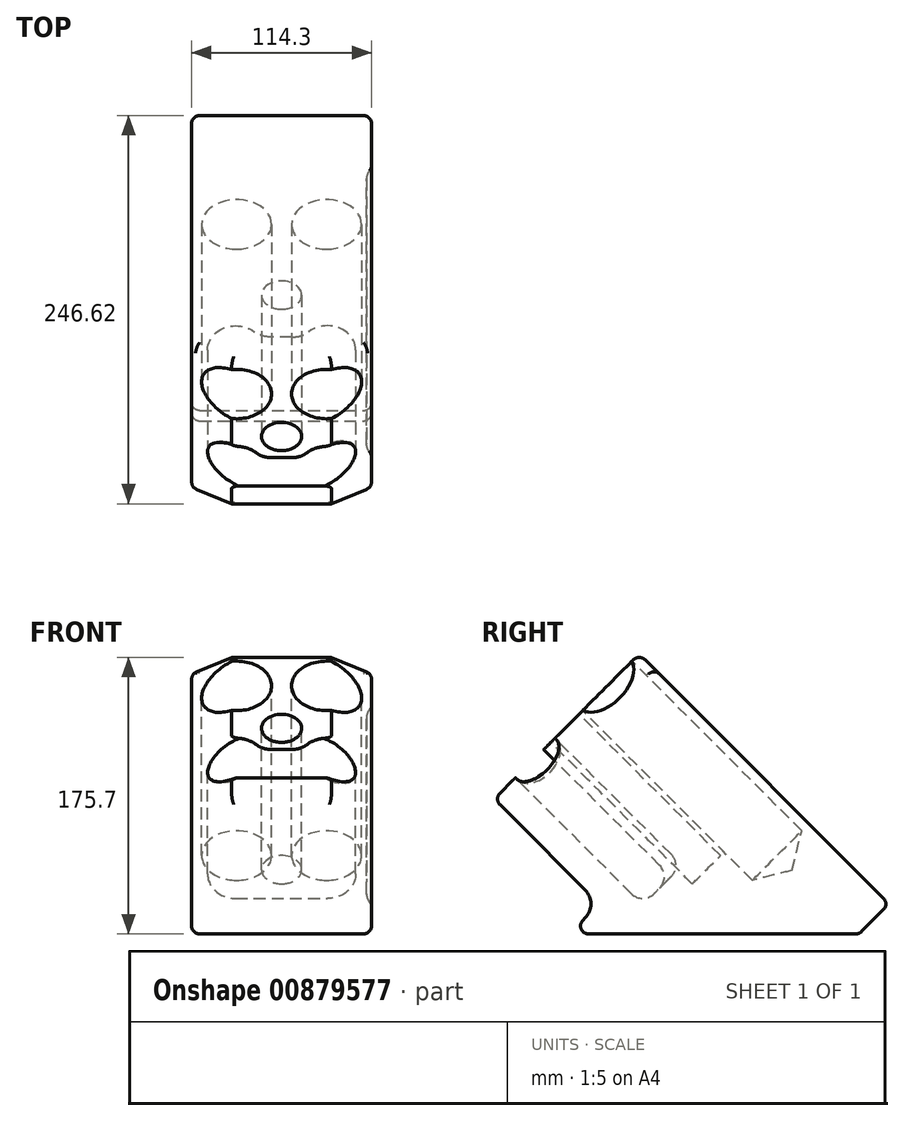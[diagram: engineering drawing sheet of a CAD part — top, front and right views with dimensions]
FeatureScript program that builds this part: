
annotation { "Feature Type Name" : "Feature", "Feature Type Description" : "" }
export const myFeature = defineFeature(function(context is Context, id is Id, definition is map)
    precondition{}
    {
        {
            var Q0;
            Q0=qCreatedBy(makeId("Right.planeOp"),FACE);
            var sketch = newSketch(context, id + "F0", { "sketchPlane" : qUnion([Q0])});
            skLineSegment(sketch, "E0", {"start": v(-92.08, 0) * mm, "end": v(-73.02, 19.05) * mm});
            skLineSegment(sketch, "E1", {"start": v(-73.03, 19.05) * mm, "end": v(-139.7, 85.73) * mm});
            skLineSegment(sketch, "E2", {"start": v(111.13, 19.05) * mm, "end": v(-47.63, 177.8) * mm});
            skLineSegment(sketch, "E3", {"start": v(-139.7, 85.72) * mm, "end": v(-47.63, 177.8) * mm});
            skLineSegment(sketch, "E4", {"start": v(111.13, 19.05) * mm, "end": v(92.08, 0) * mm});
            skLineSegment(sketch, "E5", {"start": v(-92.08, 0) * mm, "end": v(92.08, 0) * mm});
            skSolve(sketch);
        }
        {
            var Q0;
            Q0 = qSketchRegion(id + "F0", true);
            extrude(context, id + "F1", {"entities" : qUnion([Q0]), "depth" : 57.15 * mm, "offsetDistance" : 25.4 * mm, "hasSecondDirection" : true, "secondDirectionOppositeDirection" : true, "secondDirectionDepth" : 57.15 * mm});
        }
        {
            var Q0;
            Q0=makeQuery(id+"F1.opExtrude","SWEPT_FACE",FACE,{"disambiguationData":[OSD([sQuery(id+"F0.wireOp",EDGE,"E3")])]});
            var sketch = newSketch(context, id + "F2", { "sketchPlane" : qUnion([Q0])});
            skPoint(sketch, "E6", {"position": v(28.58, 63.43) * mm});
            skPoint(sketch, "E7", {"position": v(-28.57, 63.43) * mm});
            skLineSegment(sketch, "E8", {"start": v(0, -38.17) * mm, "end": v(0, 92.05) * mm, "construction": true});
            skSolve(sketch);
        }
        {
            var Q0;
            Q0=sQuery(id+"F2.wireOp",VERTEX,"E7");
            var Q1;
            Q1=sQuery(id+"F2.wireOp",VERTEX,"E6");
            var Q2;
            Q2=makeQuery(id+"F1.opExtrude","SWEPT_BODY",BODY,{"disambiguationData":[OSD([sQuery(id+"F0.wireOp",EDGE,"E0"),sQuery(id+"F0.wireOp",EDGE,"E1"),sQuery(id+"F0.wireOp",EDGE,"E2"),sQuery(id+"F0.wireOp",EDGE,"E3"),sQuery(id+"F0.wireOp",EDGE,"E4"),sQuery(id+"F0.wireOp",EDGE,"E5")])]});
            hole(context, id + "F3", {"style" : HoleStyle.SIMPLE, "endStyle" : HoleEndStyle.BLIND, "holeDiameter" : 44.45 * mm, "majorDiameter" : 6.35 * mm, "holeDepth" : 152.4 * mm, "isTappedThrough" : true, "tappedDepth" : 12.7 * mm, "tapClearance" : 3, "startFromSketch" : true, "locations" : qUnion([Q0, Q1]), "scope" : qUnion([Q2])});
        }
        {
            var Q0;
            Q0=makeQuery(id+"F1.opExtrude","SWEPT_FACE",FACE,{"disambiguationData":[OSD([sQuery(id+"F0.wireOp",EDGE,"E3")])]});
            var sketch = newSketch(context, id + "F4", { "sketchPlane" : qUnion([Q0])});
            skLineSegment(sketch, "E9.bottom", {"start": v(-6.5, 6.28) * mm, "end": v(6.5, 6.28) * mm});
            skLineSegment(sketch, "E9.top", {"start": v(-29.2, -19.12) * mm, "end": v(29.21, -19.12) * mm});
            skArc(sketch, "E10", {"start": v(29.21, -19.12) * mm, "mid": v(45.44, 5.92) * mm, "end": v(15.96, 10.52) * mm});
            skArc(sketch, "E11", {"start": v(-15.96, 10.52) * mm, "mid": v(-45.44, 5.92) * mm, "end": v(-29.2, -19.12) * mm});
            skLineSegment(sketch, "E12", {"start": v(0, -38.17) * mm, "end": v(0, 92.05) * mm, "construction": true});
            skPoint(sketch, "E13.visualSharp", {"position": v(-13.15, 6.28) * mm});
            skArc(sketch, "E13.filletArc", {"start": v(-15.96, 10.52) * mm, "mid": v(-11.68, 7.4) * mm, "end": v(-6.5, 6.28) * mm});
            skPoint(sketch, "E14.visualSharp", {"position": v(13.15, 6.28) * mm});
            skArc(sketch, "E14.filletArc", {"start": v(6.5, 6.28) * mm, "mid": v(11.68, 7.4) * mm, "end": v(15.96, 10.52) * mm});
            skSolve(sketch);
        }
        {
            var Q0;
            Q0 = qSketchRegion(id + "F4", true);
            var Q1;
            Q1=makeQuery(id+"FqLlUFFkNcJlNkp_1.hole-0.boolean.opBoolean","COPY",FACE,{"derivedFrom":makeQuery(id+"FqLlUFFkNcJlNkp_1.hole-0.opRevolve","SWEPT_FACE",FACE,{"disambiguationData":[OSD([sQuery(id+"FqLlUFFkNcJlNkp_1.hole-0.sketch.wireOp",EDGE,"core_line_1")])]})});
            extrude(context, id + "F5", {"entities" : qUnion([Q0]), "operationType" : NewBodyOperationType.REMOVE, "oppositeDirection" : true, "depth" : 114.3 * mm, "endBoundEntityFace" : qUnion([Q1]), "offsetDistance" : 25.4 * mm});
        }
        {
            var Q0;
            Q0=makeQuery(id+"F1.opExtrude","CAP_FACE",FACE,{"disambiguationData":[OSD([sQuery(id+"F0.wireOp",EDGE,"E0"),sQuery(id+"F0.wireOp",EDGE,"E1"),sQuery(id+"F0.wireOp",EDGE,"E2"),sQuery(id+"F0.wireOp",EDGE,"E3"),sQuery(id+"F0.wireOp",EDGE,"E4"),sQuery(id+"F0.wireOp",EDGE,"E5")])],"isStart":false});
            var sketch = newSketch(context, id + "F6", { "sketchPlane" : qUnion([Q0])});
            skLineSegment(sketch, "E15", {"start": v(-47.62, 141.88) * mm, "end": v(-103.78, 85.73) * mm});
            skLineSegment(sketch, "E16", {"start": v(-103.78, 76.74) * mm, "end": v(-55.81, 28.78) * mm});
            skLineSegment(sketch, "E17", {"start": v(-47.65, 19.05) * mm, "end": v(68.85, 19.05) * mm});
            skLineSegment(sketch, "E18", {"start": v(73.34, 29.9) * mm, "end": v(-38.64, 141.88) * mm});
            skPoint(sketch, "E19.visualSharp", {"position": v(-43.13, 146.37) * mm});
            skArc(sketch, "E19.filletArc", {"start": v(-38.64, 141.88) * mm, "mid": v(-43.13, 143.74) * mm, "end": v(-47.63, 141.88) * mm});
            skPoint(sketch, "E20.visualSharp", {"position": v(-108.27, 81.23) * mm});
            skArc(sketch, "E20.filletArc", {"start": v(-103.78, 85.72) * mm, "mid": v(-105.64, 81.23) * mm, "end": v(-103.78, 76.74) * mm});
            skPoint(sketch, "E21.visualSharp", {"position": v(-53.97, 26.94) * mm});
            skArc(sketch, "E21.filletArc", {"start": v(-53.97, 24.84) * mm, "mid": v(-54.55, 26.97) * mm, "end": v(-55.81, 28.78) * mm});
            skPoint(sketch, "E22.visualSharp", {"position": v(-53.97, 19.05) * mm});
            skArc(sketch, "E22.filletArc", {"start": v(-53.98, 24.84) * mm, "mid": v(-51.94, 20.72) * mm, "end": v(-47.65, 19.05) * mm});
            skPoint(sketch, "E23.visualSharp", {"position": v(84.18, 19.05) * mm});
            skArc(sketch, "E24.filletArc", {"start": v(68.85, 19.05) * mm, "mid": v(74.72, 22.97) * mm, "end": v(73.34, 29.9) * mm});
            skSolve(sketch);
        }
        {
            var Q0;
            Q0 = qSketchRegion(id + "F6", true);
            extrude(context, id + "F7", {"entities" : qUnion([Q0]), "operationType" : NewBodyOperationType.REMOVE, "oppositeDirection" : true, "depth" : 3.17 * mm, "offsetDistance" : 25.4 * mm});
        }
        {
            var Q0;
            Q0=makeQuery(id+"F7.boolean.opBoolean","COPY",FACE,{"derivedFrom":makeQuery(id+"F7.opExtrude","CAP_FACE",FACE,{"disambiguationData":[OSD([sQuery(id+"F6.wireOp",EDGE,"E15"),sQuery(id+"F6.wireOp",EDGE,"E16"),sQuery(id+"F6.wireOp",EDGE,"7AxbsLaR-Xcft-GEoA-6Mjt-eEe8P8fqxbiq"),sQuery(id+"F6.wireOp",EDGE,"E17"),sQuery(id+"F6.wireOp",EDGE,"W5dISl3W-T3MT-1PGL-jX8X-JWsG3BONESX9"),sQuery(id+"F6.wireOp",EDGE,"E18")])],"isStart":false})});
            fillet(context, id + "F8", {"entities" : qUnion([Q0]), "radius" : 7.62 * mm, "tangentPropagation" : true, "allowEdgeOverflow" : false});
        }
        {
            var Q0;
            Q0=makeQuery(id+"F1.opExtrude","SWEPT_EDGE",EDGE,{"disambiguationData":[OSD([sQuery(id+"F0.wireOp",EDGE,"E0"),sQuery(id+"F0.wireOp",EDGE,"E1")])]});
            fillet(context, id + "F9", {"entities" : qUnion([Q0]), "radius" : 12.7 * mm, "tangentPropagation" : true, "allowEdgeOverflow" : false});
        }
        {
            var Q0;
            Q0=makeQuery(id+"F5.boolean.opBoolean","COPY",FACE,{"derivedFrom":makeQuery(id+"F5.opExtrude","CAP_FACE",FACE,{"disambiguationData":[OSD([sQuery(id+"F4.wireOp",EDGE,"E9.bottom"),sQuery(id+"F4.wireOp",EDGE,"E9.top"),sQuery(id+"F4.wireOp",EDGE,"E10"),sQuery(id+"F4.wireOp",EDGE,"E11")])],"isStart":false})});
            fillet(context, id + "F10", {"entities" : qUnion([Q0]), "radius" : 10.16 * mm, "tangentPropagation" : true, "allowEdgeOverflow" : false});
        }
        {
            var Q0;
            Q0=makeQuery(id+"F1.opExtrude","CAP_EDGE",EDGE,{"disambiguationData":[OSD([sQuery(id+"F0.wireOp",EDGE,"E3")])],"isStart":false});
            var Q1;
            Q1=makeQuery(id+"F1.opExtrude","CAP_EDGE",EDGE,{"disambiguationData":[OSD([sQuery(id+"F0.wireOp",EDGE,"E3")])],"isStart":true});
            chamfer(context, id + "F11", {"entities" : qUnion([Q0, Q1]), "chamferType" : ChamferType.OFFSET_ANGLE, "width" : 25.4 * mm, "oppositeDirection" : false, "angle" : 30 * degree, "tangentPropagation" : true});
        }
        {
            var Q0;
            Q0=makeQuery(id+"F11.opChamfer","SPLIT",FACE,{"disambiguationData":[OD(1.0)],"derivedFrom":makeQuery(id+"F1.opExtrude","SWEPT_FACE",FACE,{"disambiguationData":[OSD([sQuery(id+"F0.wireOp",EDGE,"E3")])]})});
            var sketch = newSketch(context, id + "F12", { "sketchPlane" : qUnion([Q0])});
            skCircle(sketch, "E25", {"center": v(0, 25.33) * mm, "radius": 12.7 * mm});
            skSolve(sketch);
        }
        {
            var Q0;
            Q0 = qSketchRegion(id + "F12", true);
            extrude(context, id + "F13", {"entities" : qUnion([Q0]), "operationType" : NewBodyOperationType.REMOVE, "oppositeDirection" : true, "depth" : 127 * mm, "offsetDistance" : 25.4 * mm});
        }
        {
            var Q0;
            Q0=makeQuery(id+"F1.opExtrude","SWEPT_FACE",FACE,{"disambiguationData":[OSD([sQuery(id+"F0.wireOp",EDGE,"E5")])]});
            var Q1;
            Q1=makeQuery(id+"F1.opExtrude","SWEPT_FACE",FACE,{"disambiguationData":[OSD([sQuery(id+"F0.wireOp",EDGE,"E1")])]});
            var Q2;
            Q2=makeQuery(id+"F1.opExtrude","SWEPT_FACE",FACE,{"disambiguationData":[OSD([sQuery(id+"F0.wireOp",EDGE,"E2")])]});
            var Q3;
            Q3=makeQuery(id+"F1.opExtrude","CAP_FACE",FACE,{"disambiguationData":[OSD([sQuery(id+"F0.wireOp",EDGE,"E0"),sQuery(id+"F0.wireOp",EDGE,"E1"),sQuery(id+"F0.wireOp",EDGE,"E2"),sQuery(id+"F0.wireOp",EDGE,"E3"),sQuery(id+"F0.wireOp",EDGE,"E4"),sQuery(id+"F0.wireOp",EDGE,"E5")])],"isStart":true});
            var Q4;
            Q4=makeQuery(id+"F1.opExtrude","CAP_FACE",FACE,{"disambiguationData":[OSD([sQuery(id+"F0.wireOp",EDGE,"E0"),sQuery(id+"F0.wireOp",EDGE,"E1"),sQuery(id+"F0.wireOp",EDGE,"E2"),sQuery(id+"F0.wireOp",EDGE,"E3"),sQuery(id+"F0.wireOp",EDGE,"E4"),sQuery(id+"F0.wireOp",EDGE,"E5")])],"isStart":false});
            fillet(context, id + "F14", {"entities" : qUnion([Q0, Q1, Q2, Q3, Q4]), "radius" : 5.08 * mm, "tangentPropagation" : true, "allowEdgeOverflow" : false});
        }
        {
            var Q0;
            Q0=makeQuery(id+"F3.hole-0.boolean.opBoolean","COPY",EDGE,{"derivedFrom":makeQuery(id+"F3.hole-0.opRevolve","SWEPT_EDGE",EDGE,{"disambiguationData":[OSD([sQuery(id+"F3.hole-0.sketch.wireOp",EDGE,"core_line_2"),sQuery(id+"F3.hole-0.sketch.wireOp",EDGE,"core_line_3")])]})});
            var Q1;
            Q1=makeQuery(id+"F11.opChamfer","BLEND_EDGE",EDGE,{"blendedFrom":[makeQuery(id+"F1.opExtrude","CAP_EDGE",EDGE,{"disambiguationData":[OSD([sQuery(id+"F0.wireOp",EDGE,"E3")])],"isStart":true}),makeQuery(id+"F3.hole-0.boolean.opBoolean","COPY",FACE,{"derivedFrom":makeQuery(id+"F3.hole-0.opRevolve","SWEPT_FACE",FACE,{"disambiguationData":[OSD([sQuery(id+"F3.hole-0.sketch.wireOp",EDGE,"core_line_2")])]})})],"blendedInto":[makeQuery(id+"F3.hole-0.boolean.opBoolean","COPY",FACE,{"derivedFrom":makeQuery(id+"F3.hole-0.opRevolve","SWEPT_FACE",FACE,{"disambiguationData":[OSD([sQuery(id+"F3.hole-0.sketch.wireOp",EDGE,"core_line_2")])]})})]});
            var Q2;
            Q2=makeQuery(id+"F3.hole-1.boolean.opBoolean","COPY",EDGE,{"derivedFrom":makeQuery(id+"F3.hole-1.opRevolve","SWEPT_EDGE",EDGE,{"disambiguationData":[OSD([sQuery(id+"F3.hole-1.sketch.wireOp",EDGE,"core_line_2"),sQuery(id+"F3.hole-1.sketch.wireOp",EDGE,"core_line_3")])]})});
            var Q3;
            Q3=makeQuery(id+"F11.opChamfer","BLEND_EDGE",EDGE,{"blendedFrom":[makeQuery(id+"F1.opExtrude","CAP_EDGE",EDGE,{"disambiguationData":[OSD([sQuery(id+"F0.wireOp",EDGE,"E3")])],"isStart":false}),makeQuery(id+"F3.hole-1.boolean.opBoolean","COPY",FACE,{"derivedFrom":makeQuery(id+"F3.hole-1.opRevolve","SWEPT_FACE",FACE,{"disambiguationData":[OSD([sQuery(id+"F3.hole-1.sketch.wireOp",EDGE,"core_line_2")])]})})],"blendedInto":[makeQuery(id+"F3.hole-1.boolean.opBoolean","COPY",FACE,{"derivedFrom":makeQuery(id+"F3.hole-1.opRevolve","SWEPT_FACE",FACE,{"disambiguationData":[OSD([sQuery(id+"F3.hole-1.sketch.wireOp",EDGE,"core_line_2")])]})})]});
            var Q4;
            Q4=makeQuery(id+"F13.boolean.opBoolean","COPY",EDGE,{"derivedFrom":makeQuery(id+"F13.opExtrude","CAP_EDGE",EDGE,{"disambiguationData":[OSD([sQuery(id+"F12.wireOp",EDGE,"E25")])],"isStart":true})});
            var Q5;
            Q5=makeQuery(id+"F5.boolean.opBoolean","COPY",EDGE,{"derivedFrom":makeQuery(id+"F5.opExtrude","CAP_EDGE",EDGE,{"disambiguationData":[OSD([sQuery(id+"F4.wireOp",EDGE,"E9.bottom")])],"isStart":true})});
            var Q6;
            Q6=makeQuery(id+"F11.opChamfer","BLEND_EDGE",EDGE,{"blendedFrom":[makeQuery(id+"F1.opExtrude","CAP_EDGE",EDGE,{"disambiguationData":[OSD([sQuery(id+"F0.wireOp",EDGE,"E3")])],"isStart":false}),makeQuery(id+"F5.boolean.opBoolean","COPY",FACE,{"derivedFrom":makeQuery(id+"F5.opExtrude","SWEPT_FACE",FACE,{"disambiguationData":[OSD([sQuery(id+"F4.wireOp",EDGE,"E10")])]})})],"blendedInto":[makeQuery(id+"F5.boolean.opBoolean","COPY",FACE,{"derivedFrom":makeQuery(id+"F5.opExtrude","SWEPT_FACE",FACE,{"disambiguationData":[OSD([sQuery(id+"F4.wireOp",EDGE,"E10")])]})})]});
            var Q7;
            Q7=makeQuery(id+"F11.opChamfer","BLEND_EDGE",EDGE,{"blendedFrom":[makeQuery(id+"F1.opExtrude","CAP_EDGE",EDGE,{"disambiguationData":[OSD([sQuery(id+"F0.wireOp",EDGE,"E3")])],"isStart":true}),makeQuery(id+"F5.boolean.opBoolean","COPY",FACE,{"derivedFrom":makeQuery(id+"F5.opExtrude","SWEPT_FACE",FACE,{"disambiguationData":[OSD([sQuery(id+"F4.wireOp",EDGE,"E11")])]})})],"blendedInto":[makeQuery(id+"F5.boolean.opBoolean","COPY",FACE,{"derivedFrom":makeQuery(id+"F5.opExtrude","SWEPT_FACE",FACE,{"disambiguationData":[OSD([sQuery(id+"F4.wireOp",EDGE,"E11")])]})})]});
            var Q8;
            Q8=makeQuery(id+"F5.boolean.opBoolean","COPY",EDGE,{"derivedFrom":makeQuery(id+"F5.opExtrude","CAP_EDGE",EDGE,{"disambiguationData":[OSD([sQuery(id+"F4.wireOp",EDGE,"E9.top")])],"isStart":true})});
            fillet(context, id + "F15", {"entities" : qUnion([Q0, Q1, Q2, Q3, Q4, Q5, Q6, Q7, Q8]), "radius" : 2.54 * mm, "tangentPropagation" : true, "allowEdgeOverflow" : false});
        }
    });
